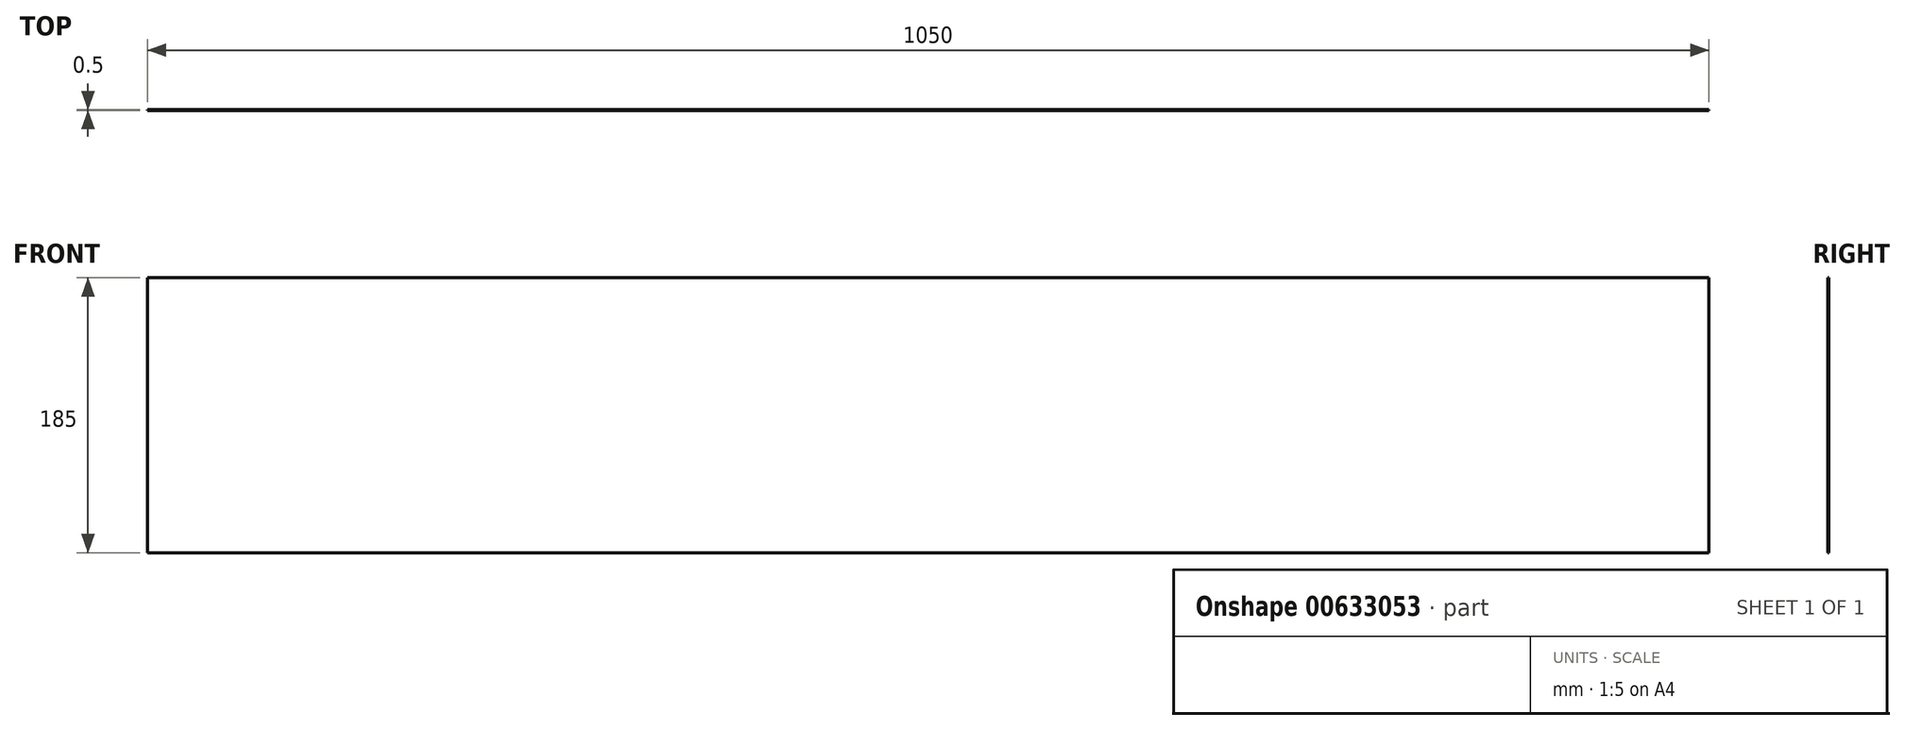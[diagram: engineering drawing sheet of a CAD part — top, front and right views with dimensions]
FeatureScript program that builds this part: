
annotation { "Feature Type Name" : "Feature", "Feature Type Description" : "" }
export const myFeature = defineFeature(function(context is Context, id is Id, definition is map)
    precondition{}
    {
        {
            var Q0;
            Q0=qCreatedBy(makeId("Front.planeOp"),FACE);
            var sketch = newSketch(context, id + "F0", { "sketchPlane" : qUnion([Q0])});
            skLineSegment(sketch, "E0.bottom", {"start": v(525, 92.5) * mm, "end": v(-525, 92.5) * mm});
            skLineSegment(sketch, "E0.top", {"start": v(525, -92.5) * mm, "end": v(-525, -92.5) * mm});
            skLineSegment(sketch, "E0.left", {"start": v(525, 92.5) * mm, "end": v(525, -92.5) * mm});
            skLineSegment(sketch, "E0.right", {"start": v(-525, 92.5) * mm, "end": v(-525, -92.5) * mm});
            skPoint(sketch, "E0.middle", {"position": v(0, 0) * mm});
            skSolve(sketch);
        }
        {
            var Q0;
            Q0=makeQuery(id+"F0.imprint","IMPRINT",FACE,{"disambiguationData":[TD([[makeQuery(id+"F0.imprint","IMPRINT",EDGE,{"derivedFrom":sQuery(id+"F0.wireOp",EDGE,"E0.bottom")}),1.0]])]});
            extrude(context, id + "F1", {"entities" : qUnion([Q0]), "depth" : 0.5 * mm, "offsetDistance" : 25 * mm});
        }
    });
